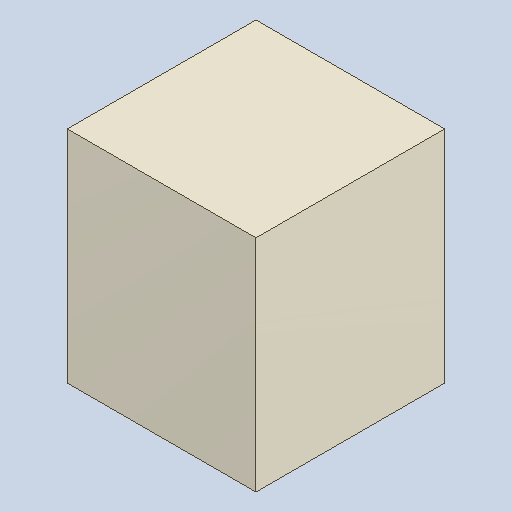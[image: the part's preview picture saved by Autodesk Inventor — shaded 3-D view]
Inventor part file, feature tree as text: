
AUTODESK INVENTOR PART (.ipt)
format: ipt  version: 2023.4 (Build 274418000, 418)  size: 82,944 bytes
history: native  units: mm
features: extrude x1
ambient origin geometry x8: Origin, YZ Plane, XZ Plane, XY Plane, X Axis, Y Axis, Z Axis, Center Point
bodies: Solid1 (feature_tree)
feature tree (1):
  extrude  "Extruded_32"  [1 undecoded]
note: 1 required parameter value undecoded (feature->parameter linkage not recoverable at this tier; creation-order binding heuristic only, values carry confidence <= 0.55)
